AUTODESK INVENTOR PART (.ipt)
format: ipt  version: 2016 (Build 200138000, 138)  size: 311,808 bytes
history: native  units: mm (DEFAULTED — no unit token found)
features: other x30, plane x6, sketch x6, sweep x6
ambient origin geometry x8: Origin, YZ Plane, XZ Plane, XY Plane, X Axis, Y Axis, Z Axis, Center Point
bodies: Body1 (feature_tree), Body2 (feature_tree), Body3 (feature_tree), Body4 (feature_tree), Body5 (feature_tree), Body6 (feature_tree)
feature tree (48):
  other  "Work Point1"
  other  "Work Point2"
  other  "Wire1"
  other  "Work Point3"
  other  "Work Point4"
  other  "Wire2"
  other  "Work Point5"
  other  "Work Point6"
  other  "Wire3"
  other  "Work Point7"
  other  "Work Point8"
  other  "Work Point9"
  plane  "Work Plane1"
  plane  "Work Plane2"
  plane  "Work Plane3"
  other  "Work Point10"
  other  "Work Point11"
  other  "Wire4"
  other  "Work Point12"
  other  "Work Point13"
  other  "Wire5"
  other  "Work Point14"
  other  "Work Point15"
  other  "Wire6"
  other  "Work Point16"
  other  "Work Point17"
  other  "Work Point18"
  plane  "Work Plane4"
  plane  "Work Plane5"
  plane  "Work Plane6"
  sketch  "Sketch1"  dims[d0=0.0mm d1=0.0mm d2=0.0mm d3=0.0mm]
  other  "Srf1"
  sketch  "Sketch2"  dims[d4=0.0mm d5=0.0mm d6=0.0mm d7=0.0mm]
  other  "Srf2"
  sketch  "Sketch3"  dims[d8=0.0mm d9=0.0mm d10=0.0mm d11=0.0mm]
  other  "Srf3"
  sketch  "Sketch4"
  other  "Srf4"
  sketch  "Sketch5"
  other  "Srf5"
  sketch  "Sketch6"
  other  "Srf6"
  sweep  "SweepSrf1"
  sweep  "SweepSrf2"
  sweep  "SweepSrf3"
  sweep  "SweepSrf4"
  sweep  "SweepSrf5"
  sweep  "SweepSrf6"
